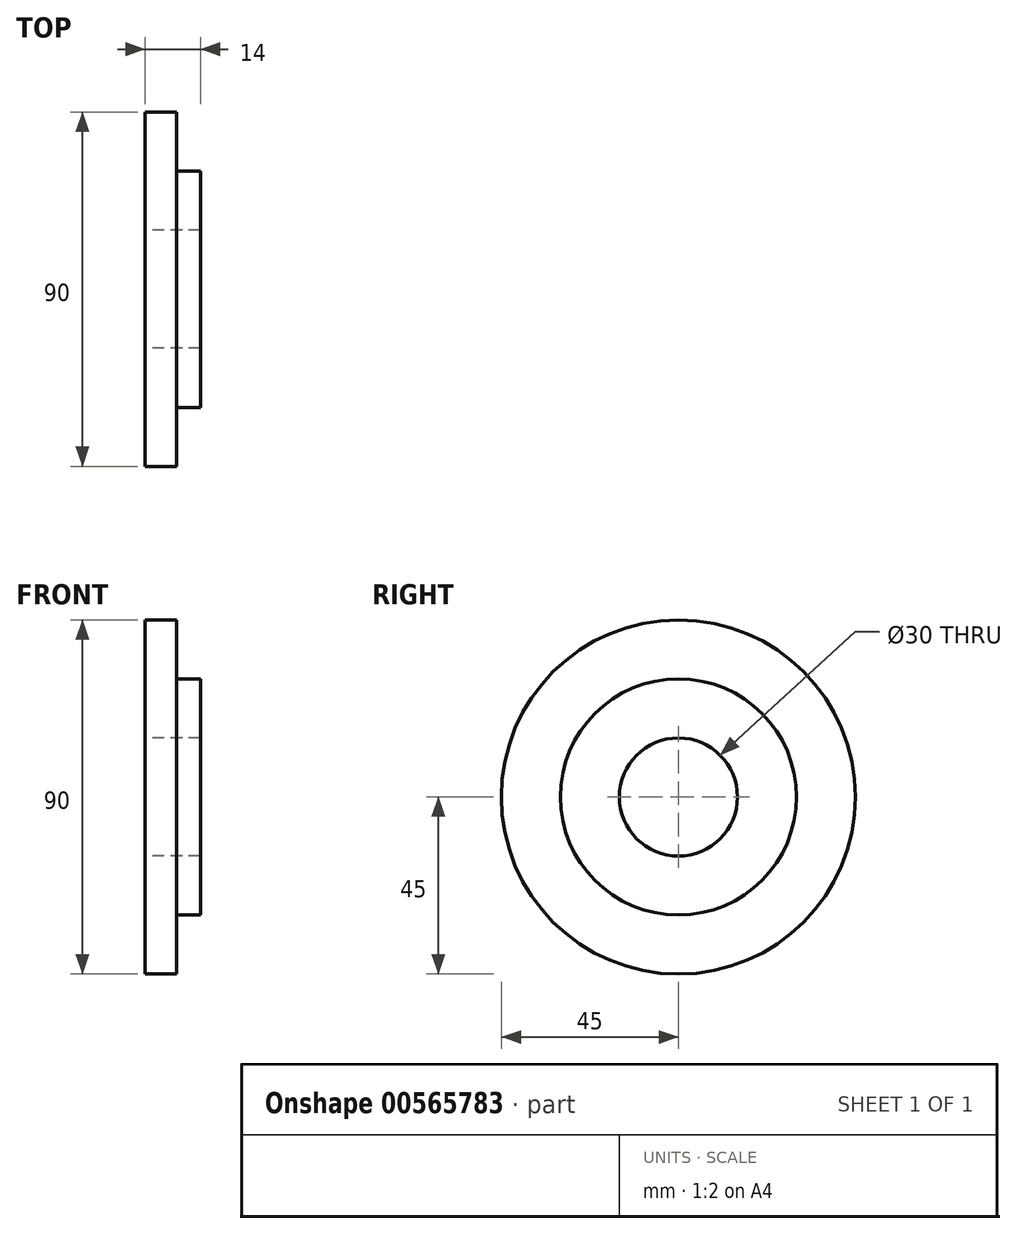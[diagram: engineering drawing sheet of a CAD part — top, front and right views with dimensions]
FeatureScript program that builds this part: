
annotation { "Feature Type Name" : "Feature", "Feature Type Description" : "" }
export const myFeature = defineFeature(function(context is Context, id is Id, definition is map)
    precondition{}
    {
        {
            var Q0;
            Q0=qCreatedBy(makeId("Front.planeOp"),FACE);
            var sketch = newSketch(context, id + "F0", { "sketchPlane" : qUnion([Q0])});
            skLineSegment(sketch, "E0.bottom", {"start": v(0, 45) * mm, "end": v(8, 45) * mm});
            skLineSegment(sketch, "E0.top", {"start": v(0, 15) * mm, "end": v(8, 15) * mm});
            skLineSegment(sketch, "E0.left", {"start": v(0, 45) * mm, "end": v(0, 15) * mm});
            skLineSegment(sketch, "E0.right", {"start": v(8, 45) * mm, "end": v(8, 15) * mm});
            skLineSegment(sketch, "E1.bottom", {"start": v(8, 15) * mm, "end": v(14, 15) * mm});
            skLineSegment(sketch, "E1.top", {"start": v(8, 30) * mm, "end": v(14, 30) * mm});
            skLineSegment(sketch, "E1.left", {"start": v(8, 15) * mm, "end": v(8, 30) * mm});
            skLineSegment(sketch, "E1.right", {"start": v(14, 15) * mm, "end": v(14, 30) * mm});
            skLineSegment(sketch, "E2", {"start": v(-19.07, 0) * mm, "end": v(59.83, 0) * mm, "construction": true});
            skSolve(sketch);
        }
        {
            var Q0;
            Q0=makeQuery(id+"F0.imprint","IMPRINT",FACE,{"disambiguationData":[TD([[makeQuery(id+"F0.imprint","IMPRINT",EDGE,{"derivedFrom":sQuery(id+"F0.wireOp",EDGE,"E0.bottom")}),-1.0]])]});
            var Q1;
            Q1=makeQuery(id+"F0.imprint","IMPRINT",FACE,{"disambiguationData":[TD([[makeQuery(id+"F0.imprint","IMPRINT",EDGE,{"derivedFrom":sQuery(id+"F0.wireOp",EDGE,"E1.bottom")}),1.0]])]});
            var Q2;
            Q2=sQuery(id+"F0.wireOp",EDGE,"E1.right");
            var Q3;
            Q3=sQuery(id+"F0.wireOp",EDGE,"E1.left");
            var Q4;
            Q4=sQuery(id+"F0.wireOp",EDGE,"E1.top");
            var Q5;
            Q5=sQuery(id+"F0.wireOp",EDGE,"E1.bottom");
            var Q6;
            Q6=sQuery(id+"F0.wireOp",EDGE,"E0.right");
            var Q7;
            Q7=sQuery(id+"F0.wireOp",EDGE,"E0.left");
            var Q8;
            Q8=sQuery(id+"F0.wireOp",EDGE,"E0.top");
            var Q9;
            Q9=sQuery(id+"F0.wireOp",EDGE,"E0.bottom");
            var Q10;
            Q10=sQuery(id+"F0.wireOp",EDGE,"E2");
            revolve(context, id + "F1", {"entities" : qUnion([Q0, Q1]), "surfaceEntities" : qUnion([Q2, Q3, Q4, Q5, Q6, Q7, Q8, Q9]), "axis" : qUnion([Q10]), "revolveType" : RevolveType.FULL});
        }
    });
